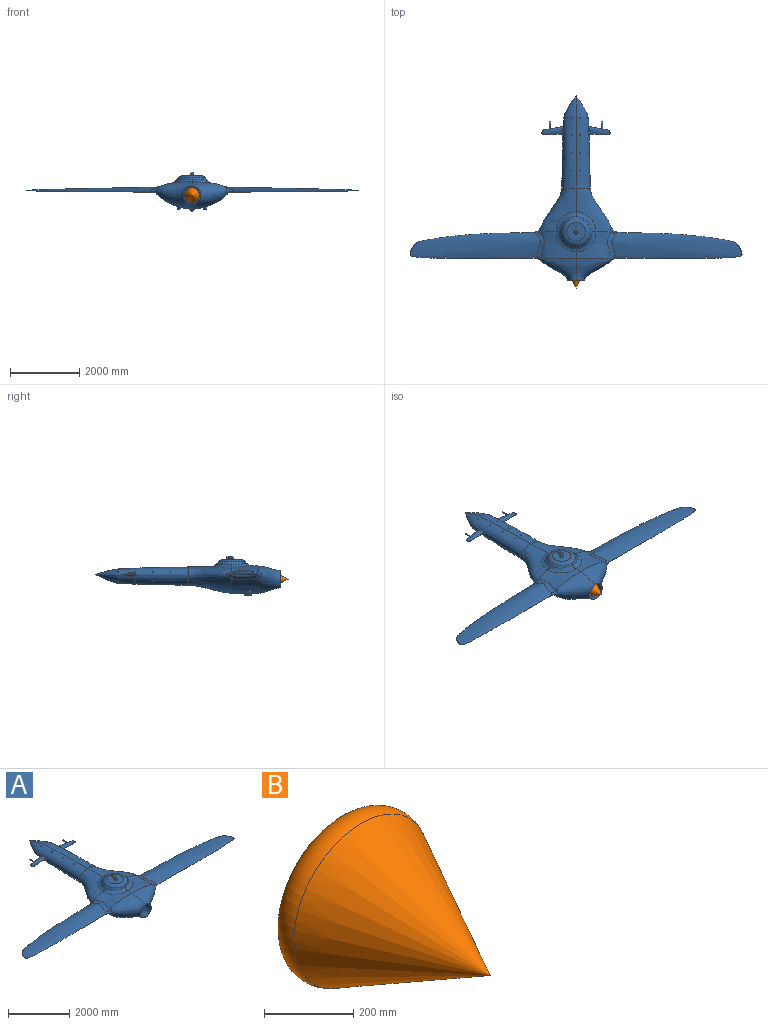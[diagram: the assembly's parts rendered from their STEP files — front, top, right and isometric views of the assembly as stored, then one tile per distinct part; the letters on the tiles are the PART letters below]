
ASSEMBLY  parts=2 mates=1
PART A: 187 faces, bbox 13590x5334x1155.7 mm
  f0: bspline ~1270x1036.44mm, area 1946429.3mm2, adj f1,f100,f101,f102,f103,f104,f105,f106
  f1: extruded ~994.99x762mm, area 844089.4mm2, adj f0,f2,f19,f64,f65,f82
  f2: sphere r=50.8mm, area 23373mm2, adj f1,f3,f7,f11,f15
  f3: cylinder r=12.7mm len=108.81mm, axis (0,1,0), area 8156.4mm2, adj f2,f4
  f4: torus R=6.35mm, axis (0,-1,0), area 651.3mm2, adj f3,f5
  f5: cylinder r=6.35mm len=110.15mm, axis (0,1,0), area 4270.5mm2, adj f4,f6
  f6: sphere r=50.8mm, area 141.2mm2, adj f5
  f7: cylinder r=12.7mm len=110.32mm, axis (0,1,0), area 8224.9mm2, adj f2,f8
  f8: torus R=6.35mm, axis (0,-1,0), area 651.3mm2, adj f7,f9
  f9: cylinder r=6.35mm len=111.23mm, axis (0,1,0), area 4302.2mm2, adj f8,f10
  f10: sphere r=50.8mm, area 143.8mm2, adj f9
  f11: cylinder r=12.7mm len=104.3mm, axis (0,1,0), area 8323mm2, adj f2,f12
  f12: torus R=6.35mm, axis (0,-1,0), area 651.3mm2, adj f11,f13
  f13: cylinder r=6.35mm len=105.08mm, axis (0,1,0), area 4192.6mm2, adj f12,f14
  f14: sphere r=50.8mm, area 134.4mm2, adj f13
  f15: cylinder r=12.7mm len=105.74mm, axis (0,1,0), area 8437.9mm2, adj f2,f16
  f16: torus R=6.35mm, axis (0,-1,0), area 651.3mm2, adj f15,f17
  f17: cylinder r=6.35mm len=107.99mm, axis (0,1,0), area 4208.2mm2, adj f16,f18
  f18: sphere r=50.8mm, area 136.5mm2, adj f17
  f19: bspline ~1036.35x785.31mm, area 1162564.2mm2, adj f1,f20,f24,f25,f61,f104
  f20: extruded ~254x186.24mm, area 53098mm2, adj f19,f21,f23,f24
  f21: plane 508x508mm, normal (0,-1,0), area 202688.6mm2, adj f20,f22,f23,f24
  f22: extruded ~426.72x254mm, area 149586.4mm2, adj f21,f23,f24,f25
  f23: extruded ~254x186.24mm, area 53097.8mm2, adj f20,f21,f22,f25
  f24: extruded ~426.72x254mm, area 149583.4mm2, adj f19,f20,f21,f22
  f25: bspline ~1036.35x785.31mm, area 1162564.2mm2, adj f19,f22,f23,f26,f34,f82
  f26: bspline ~219.19x194.73mm, area 35438.6mm2, adj f25,f27,f32,f33
  f27: bspline ~801.64x242.2mm, area 105520.1mm2, adj f26,f28,f32,f34
  f28: bspline ~184.57x142.76mm, area 9728.7mm2, adj f27,f29,f32,f106
  f29: bspline ~246.85x202.34mm, area 17713.6mm2, adj f28,f30,f32,f106
  f30: bspline ~241.76x196.6mm, area 19705.3mm2, adj f29,f31,f32,f106
  f31: bspline ~209.18x108.47mm, area 6364mm2, adj f30,f32,f33,f106
  f32: bspline ~6258.15x1191.53mm, area 4868483mm2, adj f26,f27,f28,f29,f30,f31,f33
  f33: bspline ~782.53x223.32mm, area 161761.5mm2, adj f26,f31,f32,f82
  f34: extruded ~985.57x762mm, area 505866.8mm2, adj f25,f27,f35,f104,f106
  f35: bspline ~618.36x584.03mm, area 126947.2mm2, adj f34,f36,f37,f38
  f36: bspline ~588.86x581.18mm, area 123308.8mm2, adj f35,f38,f105,f106
  f37: bspline ~618.36x584.85mm, area 126946.2mm2, adj f35,f38,f104,f105
  f38: sphere r=539.36mm, area 214399.3mm2, adj f35,f36,f37,f39,f105
  f39: torus R=266.46mm, axis (0,0,1), area 311016.1mm2, adj f38,f40
  f40: plane 532.92x532.92mm, normal (0,0,1), area 210384.4mm2, adj f39,f41
  f41: cylinder r=63.5mm len=127mm, axis (0,0,-1), area 86.1mm2, adj f40,f42
  f42: torus R=38.1mm, axis (0,0,1), area 13604.9mm2, adj f41,f43
  f43: plane 76.2x76.2mm, normal (0,0,1), area 257.2mm2, adj f42,f44
  f44: sphere r=50.8mm, area 25095mm2, adj f43,f45,f49,f53,f57
  f45: cylinder r=12.7mm len=106.26mm, axis (0,-1,0), area 8044.5mm2, adj f44,f46
  f46: torus R=6.35mm, axis (0,-1,0), area 651.3mm2, adj f45,f47
  f47: cylinder r=6.35mm len=108.31mm, axis (0,-1,0), area 4234.8mm2, adj f46,f48
  f48: sphere r=50.8mm, area 137.2mm2, adj f47
  f49: cylinder r=12.7mm len=106.26mm, axis (0,-1,0), area 8043.8mm2, adj f44,f50
  f50: torus R=6.35mm, axis (0,-1,0), area 651.3mm2, adj f49,f51
  f51: cylinder r=6.35mm len=108.31mm, axis (0,-1,0), area 4234.8mm2, adj f50,f52
  f52: sphere r=50.8mm, area 137.2mm2, adj f51
  f53: cylinder r=12.7mm len=107.75mm, axis (0,-1,0), area 8105.8mm2, adj f44,f54
  f54: torus R=6.35mm, axis (0,-1,0), area 651.3mm2, adj f53,f55
  f55: cylinder r=6.35mm len=109.39mm, axis (0,-1,0), area 4247.9mm2, adj f54,f56
  f56: sphere r=50.8mm, area 138.5mm2, adj f55
  f57: cylinder r=12.7mm len=107.75mm, axis (0,-1,0), area 8107.9mm2, adj f44,f58
  f58: torus R=6.35mm, axis (0,-1,0), area 651.3mm2, adj f57,f59
  f59: cylinder r=6.35mm len=109.39mm, axis (0,-1,0), area 4248.2mm2, adj f58,f60
  f60: sphere r=50.8mm, area 139.2mm2, adj f59
  f61: bspline ~219.19x194.74mm, area 35443mm2, adj f19,f62,f63,f64
  f62: bspline ~794.61x241.93mm, area 105520.3mm2, adj f61,f63,f103,f104
  f63: bspline ~6258.15x1191.53mm, area 4867081.1mm2, adj f61,f62,f64,f100,f101,f102,f103
  f64: bspline ~777.24x222.07mm, area 161735.1mm2, adj f1,f61,f63,f100
  f65: sphere r=50.8mm, area 24215.9mm2, adj f1,f66,f70,f74,f78,f82
  f66: cylinder r=12.7mm len=112.81mm, axis (0,-1,0), area 8336.5mm2, adj f65,f67
  f67: torus R=6.35mm, axis (0,-1,0), area 651.3mm2, adj f66,f68
  f68: cylinder r=6.35mm len=112.95mm, axis (0,-1,0), area 4353.5mm2, adj f67,f69
  f69: sphere r=50.8mm, area 146.5mm2, adj f68
  f70: cylinder r=12.7mm len=112.81mm, axis (0,-1,0), area 8337.9mm2, adj f65,f71
  f71: torus R=6.35mm, axis (0,-1,0), area 651.3mm2, adj f70,f72
  f72: cylinder r=6.35mm len=112.95mm, axis (0,-1,0), area 4353.5mm2, adj f71,f73
  f73: sphere r=50.8mm, area 146.5mm2, adj f72
  f74: cylinder r=12.7mm len=103.69mm, axis (0,-1,0), area 7933.1mm2, adj f65,f75
  f75: torus R=6.35mm, axis (0,-1,0), area 651.3mm2, adj f74,f76
  f76: cylinder r=6.35mm len=106.47mm, axis (0,-1,0), area 4166.3mm2, adj f75,f77
  f77: sphere r=50.8mm, area 132mm2, adj f76
  f78: cylinder r=12.7mm len=103.69mm, axis (0,-1,0), area 7932.9mm2, adj f65,f79
  f79: torus R=6.35mm, axis (0,-1,0), area 651.3mm2, adj f78,f80
  f80: cylinder r=6.35mm len=105.21mm, axis (0,-1,0), area 4164.8mm2, adj f79,f81
  f81: sphere r=50.8mm, area 131.6mm2, adj f80
  f82: extruded ~994.98x762mm, area 838580.6mm2, adj f1,f25,f33,f65,f83,f106
  f83: sphere r=50.8mm, area 23112.9mm2, adj f82,f84,f88,f92,f96
  f84: cylinder r=12.7mm len=107.49mm, axis (0,1,0), area 8096.8mm2, adj f83,f85
  f85: torus R=6.35mm, axis (0,-1,0), area 651.3mm2, adj f84,f86
  f86: cylinder r=6.35mm len=109.2mm, axis (0,1,0), area 4242.8mm2, adj f85,f87
  f87: sphere r=50.8mm, area 139.1mm2, adj f86
  f88: cylinder r=12.7mm len=112.33mm, axis (0,1,0), area 8316.2mm2, adj f83,f89
  f89: torus R=6.35mm, axis (0,-1,0), area 651.3mm2, adj f88,f90
  f90: cylinder r=6.35mm len=112.66mm, axis (0,1,0), area 4344.3mm2, adj f89,f91
  f91: sphere r=50.8mm, area 147.3mm2, adj f90
  f92: cylinder r=12.7mm len=107.56mm, axis (0,1,0), area 8583.2mm2, adj f83,f93
  f93: torus R=6.35mm, axis (0,-1,0), area 651.3mm2, adj f92,f94
  f94: cylinder r=6.35mm len=109.38mm, axis (0,1,0), area 4248.1mm2, adj f93,f95
  f95: sphere r=50.8mm, area 139.5mm2, adj f94
  f96: cylinder r=12.7mm len=102.97mm, axis (0,1,0), area 7903mm2, adj f83,f97
  f97: torus R=6.35mm, axis (0,-1,0), area 651.3mm2, adj f96,f98
  f98: cylinder r=6.35mm len=105.95mm, axis (0,1,0), area 4151.9mm2, adj f97,f99
  f99: sphere r=50.8mm, area 132.5mm2, adj f98
  f100: bspline ~211.07x110.98mm, area 6364.3mm2, adj f0,f63,f64,f101
  f101: bspline ~241.76x196.6mm, area 19705.5mm2, adj f0,f63,f100,f102
  f102: bspline ~246.85x202.35mm, area 17713.2mm2, adj f0,f63,f101,f103
  f103: bspline ~183.46x140.65mm, area 9728.9mm2, adj f0,f62,f63,f102
  f104: extruded ~985.57x762mm, area 505865.7mm2, adj f0,f19,f34,f37,f62
  f105: bspline ~588.86x581.18mm, area 123308.8mm2, adj f0,f36,f37,f38
  f106: bspline ~1270x1036.44mm, area 1946392.5mm2, adj f0,f28,f29,f30,f31,f34,f36,f82
  f107: cylinder r=12.7mm len=106.09mm, axis (0,0,1), area 7616mm2, adj f106,f108,f112,f114
  f108: cylinder r=12.7mm len=254mm, axis (-1,0,0), area 19047.2mm2, adj f107,f109,f111,f176
  f109: cylinder r=12.7mm len=254mm, axis (0,0,1), area 19047.2mm2, adj f108,f110,f112,f113
  f110: cylinder r=12.7mm len=254mm, axis (-1,0,0), area 20268.3mm2, adj f109,f111,f172,f173
  f111: cylinder r=12.7mm len=254mm, axis (0,0,1), area 19047.2mm2, adj f108,f110,f174,f175
  f112: cylinder r=12.7mm len=207.13mm, axis (-1,0,0), area 14835.5mm2, adj f106,f107,f109,f114
  f113: cylinder r=12.7mm len=268.02mm, axis (-1,0,0), area 20180.1mm2, adj f106,f109,f114,f172
  f114: bspline ~2667x526.8mm, area 2377148.2mm2, adj f106,f107,f112,f113,f115,f124,f133,f142
  f115: cylinder r=12.7mm len=237.09mm, axis (-1,0,0), area 17739.1mm2, adj f114,f116,f167
  f116: cylinder r=12.7mm len=254mm, axis (0,0,1), area 19047.2mm2, adj f115,f117,f123,f162
  f117: cylinder r=12.7mm len=254mm, axis (-1,0,0), area 19047.2mm2, adj f116,f118,f122,f166
  f118: cylinder r=12.7mm len=254mm, axis (0,0,1), area 19047.2mm2, adj f117,f119,f121,f123
  f119: cylinder r=12.7mm len=237.99mm, axis (-1,0,0), area 17808.6mm2, adj f118,f120,f177
  f120: cylinder r=12.7mm len=114.1mm, axis (0,0,1), area 8528.6mm2, adj f119,f123,f177
  f121: cylinder r=12.7mm len=165.14mm, axis (-1,0,0), area 11467.3mm2, adj f118,f122,f177
  f122: cylinder r=12.7mm len=75.14mm, axis (0,0,1), area 5419.9mm2, adj f117,f121,f177
  f123: cylinder r=12.7mm len=254mm, axis (-1,0,0), area 19047.2mm2, adj f116,f118,f120,f167
  f124: cylinder r=12.7mm len=258.69mm, axis (-1,0,0), area 19559.6mm2, adj f114,f125,f171
  f125: cylinder r=12.7mm len=254mm, axis (0,0,1), area 19047.2mm2, adj f124,f126,f132,f142
  f126: cylinder r=12.7mm len=254mm, axis (-1,0,0), area 19047.2mm2, adj f125,f127,f131,f170
  f127: cylinder r=12.7mm len=254mm, axis (0,0,1), area 19047.2mm2, adj f126,f128,f130,f132
  f128: cylinder r=12.7mm len=260.83mm, axis (-1,0,0), area 19725.9mm2, adj f127,f129,f177
  f129: cylinder r=12.7mm len=139.91mm, axis (0,0,1), area 10588mm2, adj f128,f132,f177
  f130: cylinder r=12.7mm len=203.55mm, axis (-1,0,0), area 14698.4mm2, adj f127,f131,f177
  f131: cylinder r=12.7mm len=100.52mm, axis (0,0,1), area 7445mm2, adj f126,f130,f177
  f132: cylinder r=12.7mm len=254mm, axis (-1,0,0), area 19047.2mm2, adj f125,f127,f129,f171
  f133: cylinder r=12.7mm len=107.69mm, axis (-1,0,0), area 6456.4mm2, adj f114,f134,f164
  f134: cylinder r=12.7mm len=254mm, axis (0,0,1), area 19047.2mm2, adj f133,f135,f141,f152
  f135: cylinder r=12.7mm len=254mm, axis (-1,0,0), area 19047.2mm2, adj f134,f136,f140,f164
  f136: cylinder r=12.7mm len=254mm, axis (0,0,1), area 19047.2mm2, adj f135,f137,f139,f141
  f137: cylinder r=12.7mm len=205.34mm, axis (-1,0,0), area 14748.2mm2, adj f136,f138,f177
  f138: cylinder r=12.7mm len=82.45mm, axis (0,0,1), area 6003mm2, adj f137,f141,f177
  f139: cylinder r=12.7mm len=107.71mm, axis (-1,0,0), area 6528.5mm2, adj f136,f140,f177
  f140: cylinder r=12.7mm len=39.21mm, axis (0,0,1), area 2553mm2, adj f135,f139,f177
  f141: cylinder r=12.7mm len=254mm, axis (-1,0,0), area 19047.2mm2, adj f134,f136,f138,f165
  f142: cylinder r=12.7mm len=202.09mm, axis (-1,0,0), area 14521.6mm2, adj f114,f125,f170
  f143: bspline ~295.03x108.05mm, area 31421mm2, adj f114,f144,f150,f151
  f144: bspline ~1015.9x358.87mm, area 200607.7mm2, adj f143,f145,f146,f150,f151
  f145: torus R=7.62mm, axis (0,1,0), area 1528.2mm2, adj f144,f146
  f146: cylinder r=12.7mm len=255.27mm, axis (0,-1,0), area 17606.1mm2, adj f144,f145,f147
  f147: torus R=6.35mm, axis (0,1,0), area 651.3mm2, adj f146,f148
  f148: cylinder r=6.35mm len=139.7mm, axis (0,-1,0), area 5573.8mm2, adj f147,f149
  f149: plane 12.7x12.7mm, normal (0,1,0), area 126.7mm2, adj f148
  f150: bspline ~56.61x55.15mm, area 1675mm2, adj f114,f143,f144,f151
  f151: bspline ~59.44x54.97mm, area 1492mm2, adj f114,f143,f144,f150
  f152: cylinder r=12.7mm len=205.31mm, axis (-1,0,0), area 14745.6mm2, adj f114,f134,f165
  f153: cylinder r=12.7mm len=189.58mm, axis (-1,0,0), area 13488mm2, adj f114,f154,f168
  f154: cylinder r=12.7mm len=254mm, axis (0,0,1), area 19047.2mm2, adj f153,f155,f161,f163
  f155: cylinder r=12.7mm len=254mm, axis (-1,0,0), area 19047.2mm2, adj f154,f156,f160,f168
  f156: cylinder r=12.7mm len=254mm, axis (0,0,1), area 19047.2mm2, adj f155,f157,f159,f161
  f157: cylinder r=12.7mm len=251.55mm, axis (-1,0,0), area 18992.9mm2, adj f156,f158,f177
  f158: cylinder r=12.7mm len=131.64mm, axis (0,0,1), area 9928.3mm2, adj f157,f161,f177
  f159: cylinder r=12.7mm len=190.92mm, axis (-1,0,0), area 13656.4mm2, adj f156,f160,f177
  f160: cylinder r=12.7mm len=92.76mm, axis (0,0,1), area 6825.7mm2, adj f155,f159,f177
  f161: cylinder r=12.7mm len=254mm, axis (-1,0,0), area 19047.2mm2, adj f154,f156,f158,f169
  f162: cylinder r=12.7mm len=164.58mm, axis (-1,0,0), area 11356.2mm2, adj f114,f116,f166
  f163: cylinder r=12.7mm len=249.54mm, axis (-1,0,0), area 18836mm2, adj f114,f154,f169
  f164: cylinder r=12.7mm len=48.26mm, axis (0,0,1), area 3275.4mm2, adj f114,f133,f135
  f165: cylinder r=12.7mm len=87.14mm, axis (0,0,1), area 6446.9mm2, adj f114,f141,f152
  f166: cylinder r=12.7mm len=82.06mm, axis (0,0,1), area 5971.9mm2, adj f114,f117,f162
  f167: cylinder r=12.7mm len=116.5mm, axis (0,0,1), area 8789.2mm2, adj f114,f115,f123
  f168: cylinder r=12.7mm len=98.91mm, axis (0,0,1), area 7316.3mm2, adj f114,f153,f155
  f169: cylinder r=12.7mm len=133.64mm, axis (0,0,1), area 10157mm2, adj f114,f161,f163
  f170: cylinder r=12.7mm len=106.77mm, axis (0,0,1), area 7943.9mm2, adj f114,f126,f142
  f171: cylinder r=12.7mm len=142.71mm, axis (0,0,1), area 10881.3mm2, adj f114,f124,f132
  f172: cylinder r=12.7mm len=144.03mm, axis (0,0,1), area 10744mm2, adj f106,f110,f113,f114
  f173: cylinder r=12.7mm len=144.03mm, axis (0,0,1), area 10744mm2, adj f0,f110,f174,f177
  f174: cylinder r=12.7mm len=268.02mm, axis (-1,0,0), area 20180.1mm2, adj f0,f111,f173,f177
  f175: cylinder r=12.7mm len=207.13mm, axis (-1,0,0), area 14904.7mm2, adj f0,f111,f176,f177
  f176: cylinder r=12.7mm len=106.09mm, axis (0,0,1), area 7616mm2, adj f0,f108,f175,f177
  f177: bspline ~2667x526.8mm, area 2380624.8mm2, adj f0,f114,f119,f120,f121,f122,f128,f129
  f178: bspline ~293.49x107.99mm, area 31238.3mm2, adj f177,f179,f185,f186
  f179: bspline ~1015.9x358.87mm, area 199700.6mm2, adj f178,f180,f181,f185,f186
  f180: torus R=7.62mm, axis (0,1,0), area 0mm2, adj f179,f181
  f181: cylinder r=12.7mm len=255.27mm, axis (0,-1,0), area 17599.9mm2, adj f179,f180,f182
  f182: torus R=6.35mm, axis (0,1,0), area 651.3mm2, adj f181,f183
  f183: cylinder r=6.35mm len=139.7mm, axis (0,-1,0), area 5573.8mm2, adj f182,f184
  f184: plane 12.7x12.7mm, normal (0,1,0), area 126.7mm2, adj f183
  f185: bspline ~59.53x55.14mm, area 1495.2mm2, adj f177,f178,f179,f186
  f186: bspline ~56.95x55.34mm, area 1698.5mm2, adj f177,f178,f179,f185
PART B: 3 faces, bbox 477.7x482.6x477.7 mm
  f0: plane 339.71x339.71mm, normal (0,1,0), area 90639.1mm2, adj f2
  f1: cone r=254mm half-angle=27.8deg, axis (0,1,0), area 311251.6mm2, adj f2
  f2: torus R=169.86mm, axis (0,-1,0), area 135195mm2, adj f0,f1
PLACE A t=(1095.01,6021.71,-1067.82)mm
PLACE B t=(1095.01,6224.91,-1067.84)mm
MATE fastened B.f1 <-> A.f21  axis (0,1,0) through (1095.01,941.71,-1204.15)mm
